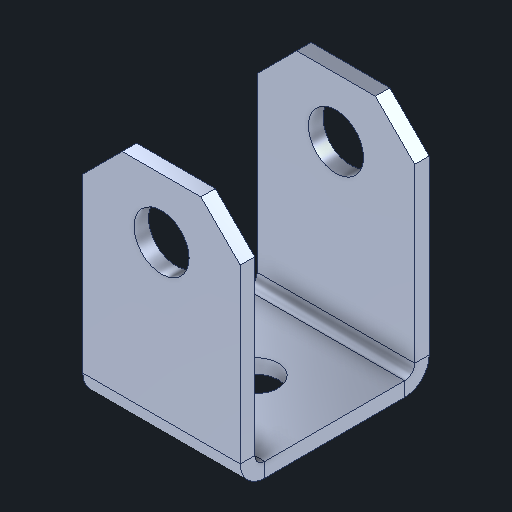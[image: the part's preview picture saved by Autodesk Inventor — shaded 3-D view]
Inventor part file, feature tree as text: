
AUTODESK INVENTOR PART (.ipt)
format: ipt  version: 2024 (Build 280153000, 153)  size: 166,400 bytes
history: native  units: in
note: dims shown in document units (in); Inventor stores cm internally (conversion verified against a paired STEP export)
features: other x2, chamfer x2
ambient origin geometry x8: Origin, YZ Plane, XZ Plane, XY Plane, X Axis, Y Axis, Z Axis, Center Point
bodies: Body1 (feature_tree)
feature tree (4):
  other  "Cylinder Mount.ipt"
  chamfer  "Chamfer1::Cylinder Mount.ipt"  Distance=0.3937in
  other  "TaggingFeature1"
  chamfer  "Chamfer1"  [1 undecoded]
note: 1 required parameter value undecoded (feature->parameter linkage not recoverable at this tier; creation-order binding heuristic only, values carry confidence <= 0.55)
